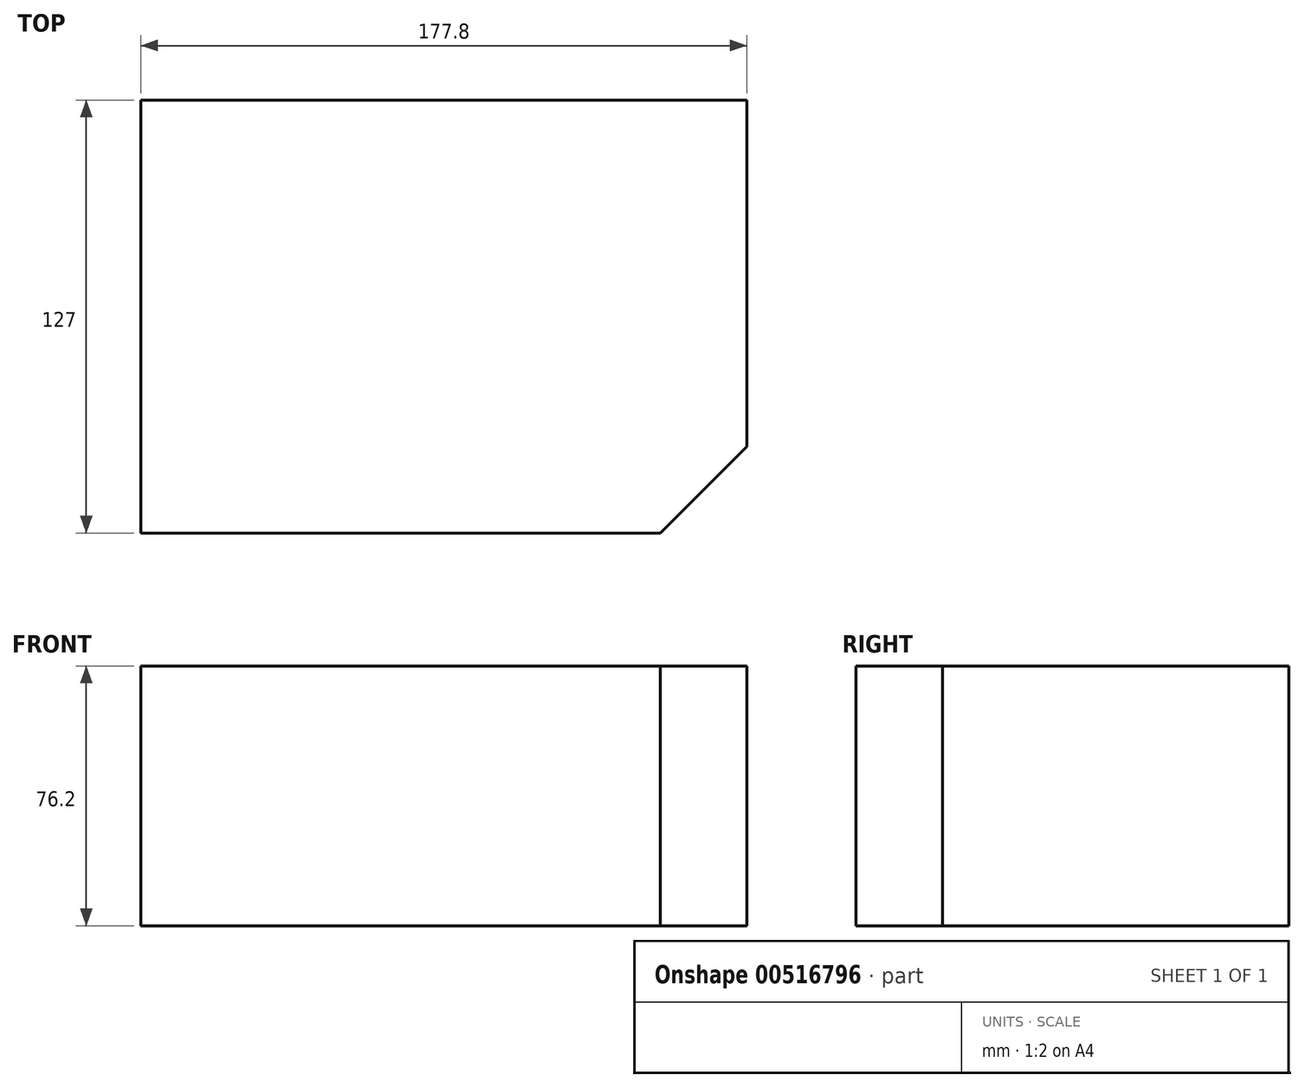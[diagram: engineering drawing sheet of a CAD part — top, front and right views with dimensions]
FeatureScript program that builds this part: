
annotation { "Feature Type Name" : "Feature", "Feature Type Description" : "" }
export const myFeature = defineFeature(function(context is Context, id is Id, definition is map)
    precondition{}
    {
        {
            var Q0;
            Q0=qCreatedBy(makeId("Top.planeOp"),FACE);
            var sketch = newSketch(context, id + "F0", { "sketchPlane" : qUnion([Q0])});
            skLineSegment(sketch, "E0.bottom", {"start": v(88.9, -63.5) * mm, "end": v(-88.9, -63.5) * mm});
            skLineSegment(sketch, "E0.top", {"start": v(88.9, 63.5) * mm, "end": v(-88.9, 63.5) * mm});
            skLineSegment(sketch, "E0.left", {"start": v(88.9, -63.5) * mm, "end": v(88.9, 63.5) * mm});
            skLineSegment(sketch, "E0.right", {"start": v(-88.9, -63.5) * mm, "end": v(-88.9, 63.5) * mm});
            skPoint(sketch, "E0.middle", {"position": v(0, 0) * mm});
            skSolve(sketch);
        }
        {
            var Q0;
            Q0 = qSketchRegion(id + "F0", true);
            extrude(context, id + "F1", {"entities" : qUnion([Q0]), "depth" : 76.2 * mm, "offsetDistance" : 25.4 * mm});
        }
        {
            var Q0;
            Q0=makeQuery(id+"F1.opExtrude","SWEPT_EDGE",EDGE,{"disambiguationData":[OSD([sQuery(id+"F0.wireOp",EDGE,"E0.bottom"),sQuery(id+"F0.wireOp",EDGE,"E0.left")])]});
            chamfer(context, id + "F2", {"entities" : qUnion([Q0]), "width" : 25.4 * mm, "tangentPropagation" : true});
        }
    });
